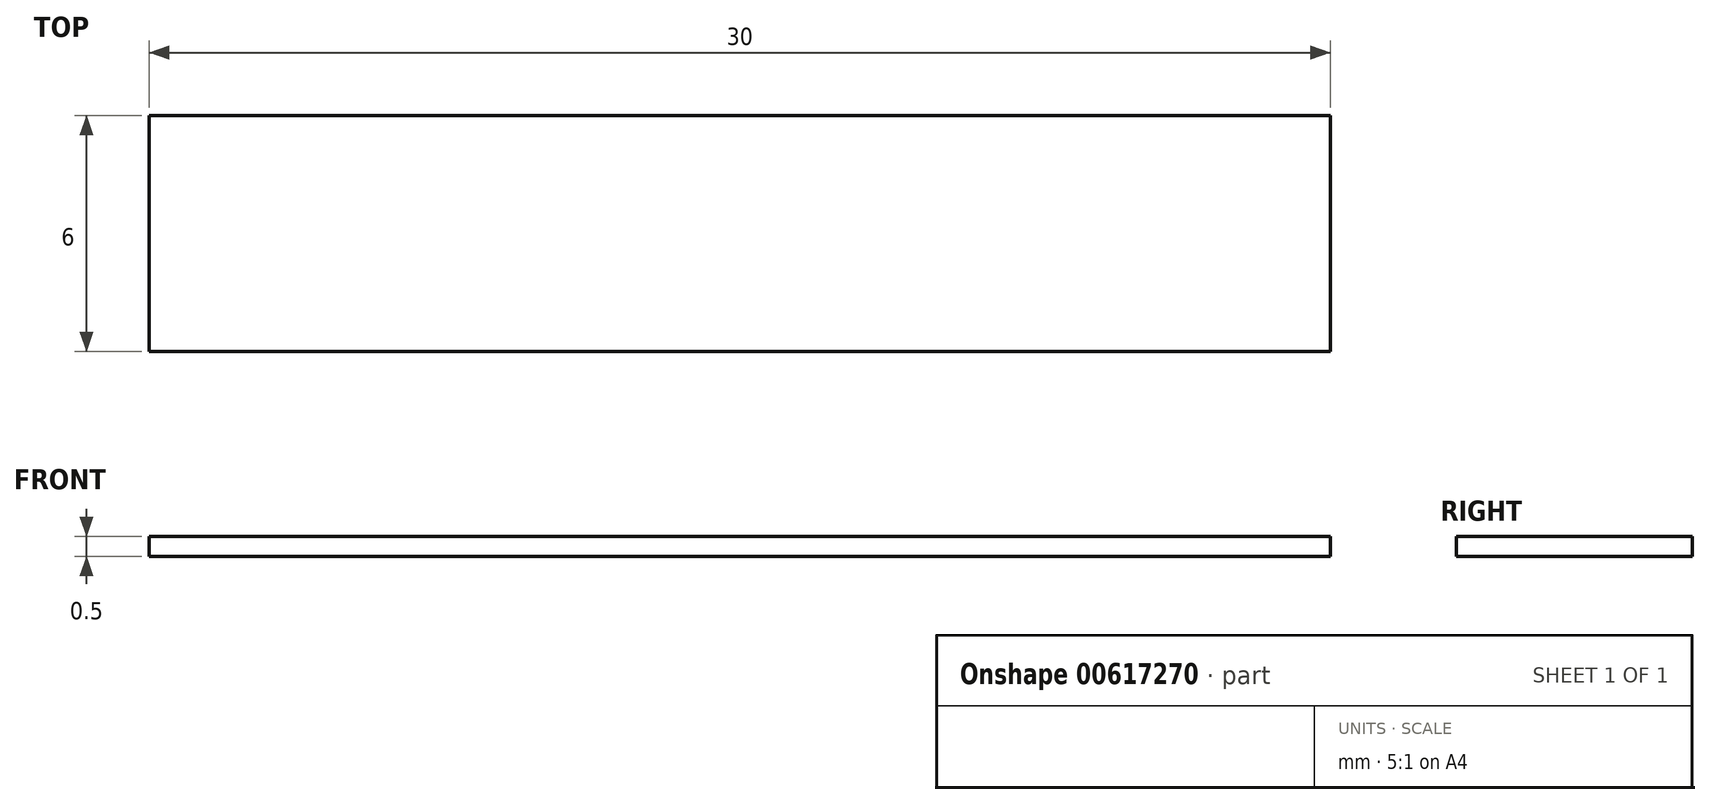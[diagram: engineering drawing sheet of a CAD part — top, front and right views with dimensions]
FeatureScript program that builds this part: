
annotation { "Feature Type Name" : "Feature", "Feature Type Description" : "" }
export const myFeature = defineFeature(function(context is Context, id is Id, definition is map)
    precondition{}
    {
        {
            var Q0;
            Q0=qCreatedBy(makeId("Top.planeOp"),FACE);
            var sketch = newSketch(context, id + "F0", { "sketchPlane" : qUnion([Q0])});
            skLineSegment(sketch, "E0.bottom", {"start": v(15, 3) * mm, "end": v(-15, 3) * mm});
            skLineSegment(sketch, "E0.top", {"start": v(15, -3) * mm, "end": v(-15, -3) * mm});
            skLineSegment(sketch, "E0.left", {"start": v(15, 3) * mm, "end": v(15, -3) * mm});
            skLineSegment(sketch, "E0.right", {"start": v(-15, 3) * mm, "end": v(-15, -3) * mm});
            skPoint(sketch, "E0.middle", {"position": v(0, 0) * mm});
            skSolve(sketch);
        }
        {
            var Q0;
            Q0=makeQuery(id+"F0.imprint","IMPRINT",FACE,{"disambiguationData":[TD([[makeQuery(id+"F0.imprint","IMPRINT",EDGE,{"derivedFrom":sQuery(id+"F0.wireOp",EDGE,"E0.bottom")}),1.0]])]});
            extrude(context, id + "F1", {"entities" : qUnion([Q0]), "depth" : 0.5 * mm, "offsetDistance" : 25 * mm});
        }
    });
